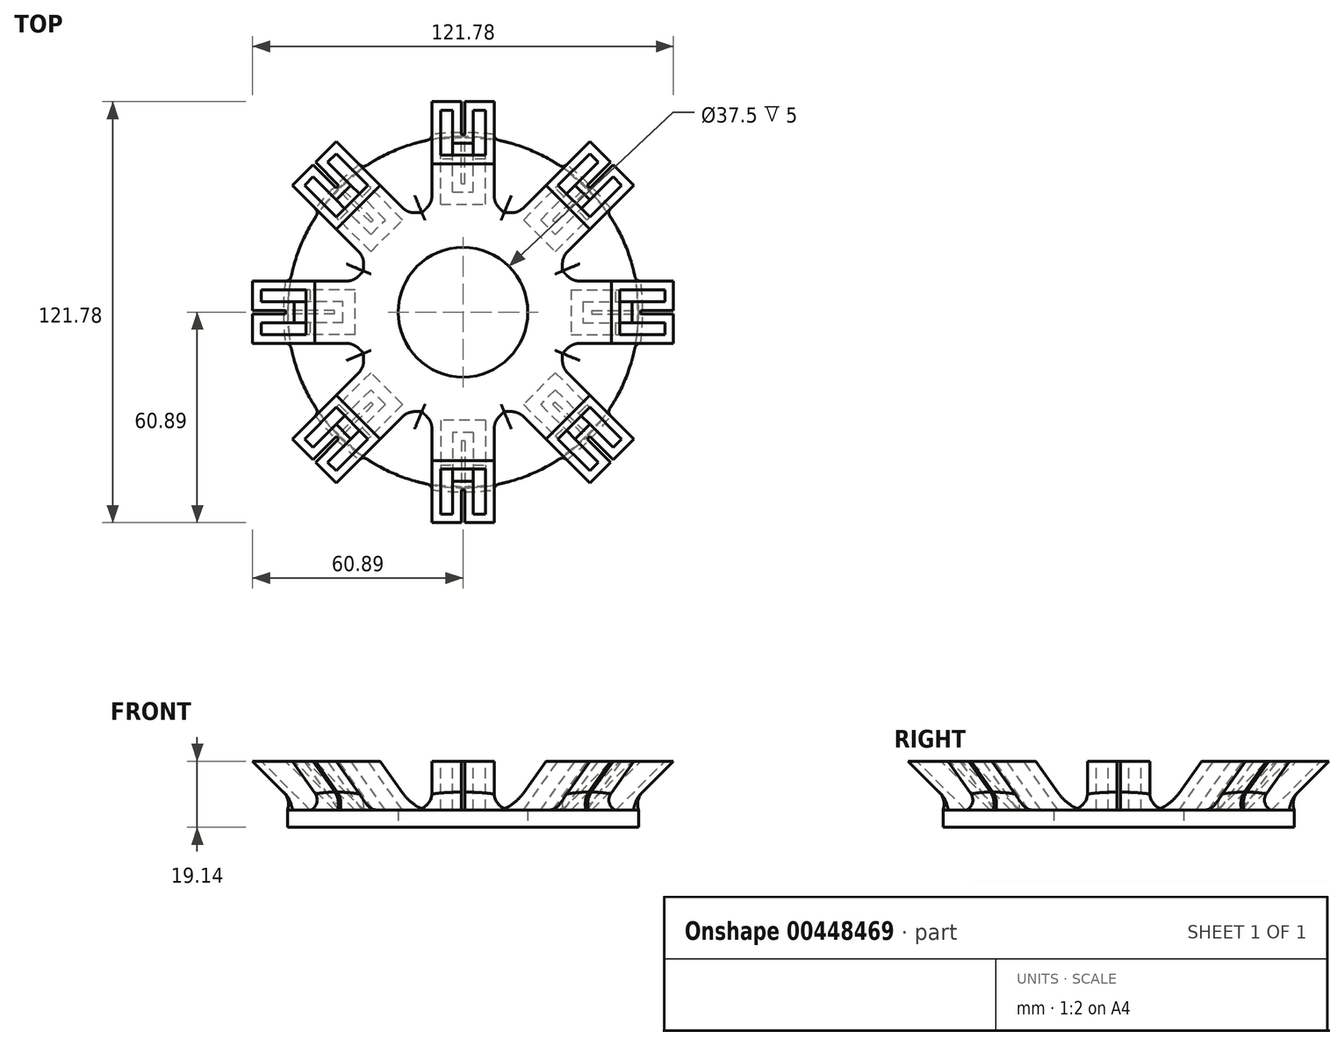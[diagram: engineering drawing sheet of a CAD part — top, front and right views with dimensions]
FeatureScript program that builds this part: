
annotation { "Feature Type Name" : "Feature", "Feature Type Description" : "" }
export const myFeature = defineFeature(function(context is Context, id is Id, definition is map)
    precondition{}
    {
        {
            var Q0;
            Q0=qCreatedBy(makeId("Top.planeOp"),FACE);
            var sketch = newSketch(context, id + "F0", { "sketchPlane" : qUnion([Q0])});
            skCircle(sketch, "E0", {"center": v(0, 0) * mm, "radius": 18.75 * mm});
            skCircle(sketch, "E1", {"center": v(0, 0) * mm, "radius": 50.8 * mm});
            skSolve(sketch);
        }
        {
            var Q0;
            Q0=makeQuery(id+"F0.imprint","IMPRINT",FACE,{"disambiguationData":[TD([[makeQuery(id+"F0.imprint","IMPRINT",EDGE,{"derivedFrom":sQuery(id+"F0.wireOp",EDGE,"E0")}),-1.0]])]});
            extrude(context, id + "F1", {"entities" : qUnion([Q0]), "depth" : 5 * mm});
        }
        {
            var Q0;
            Q0=makeQuery(id+"F1.opExtrude","CAP_FACE",FACE,{"disambiguationData":[OSD([sQuery(id+"F0.wireOp",EDGE,"E0"),sQuery(id+"F0.wireOp",EDGE,"E1")])],"isStart":false});
            var sketch = newSketch(context, id + "F2", { "sketchPlane" : qUnion([Q0])});
            skPoint(sketch, "E2", {"position": v(0, -31.75) * mm});
            skLineSegment(sketch, "E3", {"start": v(6, -31.75) * mm, "end": v(-6, -31.75) * mm});
            skLineSegment(sketch, "E4", {"start": v(6, -31.75) * mm, "end": v(6, -43.75) * mm});
            skLineSegment(sketch, "E5", {"start": v(-6, -31.75) * mm, "end": v(-6, -43.75) * mm});
            skLineSegment(sketch, "E6.0", {"start": v(-3.5, -34.25) * mm, "end": v(-3.5, -43.75) * mm});
            skLineSegment(sketch, "E6.1", {"start": v(3.5, -34.25) * mm, "end": v(-3.5, -34.25) * mm});
            skLineSegment(sketch, "E6.2", {"start": v(3.5, -34.25) * mm, "end": v(3.5, -43.75) * mm});
            skLineSegment(sketch, "E7", {"start": v(-6, -43.75) * mm, "end": v(-3.5, -43.75) * mm});
            skLineSegment(sketch, "E8", {"start": v(3.5, -43.75) * mm, "end": v(6, -43.75) * mm});
            skLineSegment(sketch, "E9.0", {"start": v(6.5, -31.25) * mm, "end": v(6.5, -44.25) * mm});
            skLineSegment(sketch, "E9.1", {"start": v(3, -44.25) * mm, "end": v(6.5, -44.25) * mm});
            skLineSegment(sketch, "E9.2", {"start": v(6.5, -31.25) * mm, "end": v(-6.5, -31.25) * mm});
            skLineSegment(sketch, "E9.3", {"start": v(3, -34.75) * mm, "end": v(3, -44.25) * mm});
            skLineSegment(sketch, "E9.4", {"start": v(-6.5, -31.25) * mm, "end": v(-6.5, -44.25) * mm});
            skLineSegment(sketch, "E9.5", {"start": v(-6.5, -44.25) * mm, "end": v(-3, -44.25) * mm});
            skLineSegment(sketch, "E9.6", {"start": v(-3, -34.75) * mm, "end": v(-3, -44.25) * mm});
            skLineSegment(sketch, "E9.7", {"start": v(3, -34.75) * mm, "end": v(-3, -34.75) * mm});
            skLineSegment(sketch, "E10.0", {"start": v(9, -28.75) * mm, "end": v(9, -46.75) * mm});
            skLineSegment(sketch, "E10.1", {"start": v(0.5, -46.75) * mm, "end": v(9, -46.75) * mm});
            skLineSegment(sketch, "E10.2", {"start": v(9, -28.75) * mm, "end": v(-9, -28.75) * mm});
            skLineSegment(sketch, "E10.3", {"start": v(0.5, -37.25) * mm, "end": v(0.5, -46.75) * mm});
            skLineSegment(sketch, "E10.4", {"start": v(-9, -28.75) * mm, "end": v(-9, -46.75) * mm});
            skLineSegment(sketch, "E10.5", {"start": v(-9, -46.75) * mm, "end": v(-0.5, -46.75) * mm});
            skLineSegment(sketch, "E10.6", {"start": v(-0.5, -37.25) * mm, "end": v(-0.5, -46.75) * mm});
            skLineSegment(sketch, "E10.7", {"start": v(0.5, -37.25) * mm, "end": v(-0.5, -37.25) * mm});
            skSolve(sketch);
        }
        {
            var Q0;
            Q0=qCreatedBy(makeId("Right.planeOp"),FACE);
            var sketch = newSketch(context, id + "F3", { "sketchPlane" : qUnion([Q0])});
            skPoint(sketch, "E11", {"position": v(-28.75, 5) * mm});
            skLineSegment(sketch, "E12", {"start": v(-28.75, 5) * mm, "end": v(-42.9, 19.14) * mm});
            skLineSegment(sketch, "E13", {"start": v(-28.75, 5) * mm, "end": v(-45.86, 5) * mm, "construction": true});
            skSolve(sketch);
        }
        {
            var Q0;
            Q0=makeQuery(id+"F2.imprint","IMPRINT",FACE,{"disambiguationData":[TD([[makeQuery(id+"F2.imprint","IMPRINT",EDGE,{"derivedFrom":sQuery(id+"F2.wireOp",EDGE,"E9.0")}),1.0]])]});
            var Q1;
            Q1=sQuery(id+"F3.wireOp",EDGE,"E12");
            sweep(context, id + "F4", {"operationType" : NewBodyOperationType.ADD, "profiles" : qUnion([Q0]), "path" : qUnion([Q1])});
        }
        {
            var Q0;
            Q0=qCreatedBy(makeId("Right.planeOp"),FACE);
            var sketch = newSketch(context, id + "F5", { "sketchPlane" : qUnion([Q0])});
            skLineSegment(sketch, "E14", {"start": v(0, 0) * mm, "end": v(0, 26.54) * mm, "construction": true});
            skSolve(sketch);
        }
        {
            var Q0;
            Q0=makeQuery(id+"F4.opSweep","CAP_EDGE",EDGE,{"disambiguationData":[OSD([sQuery(id+"F2.wireOp",EDGE,"E10.2"),sQuery(id+"F3.wireOp",VERTEX,"E12.start")])],"isStart":true});
            var Q1;
            Q1=makeQuery(id+"F4.opSweep","CAP_EDGE",EDGE,{"disambiguationData":[OSD([sQuery(id+"F2.wireOp",EDGE,"E10.0"),sQuery(id+"F3.wireOp",VERTEX,"E12.start")])],"isStart":true});
            var Q2;
            Q2=makeQuery(id+"F4.opSweep","CAP_EDGE",EDGE,{"disambiguationData":[OSD([sQuery(id+"F2.wireOp",EDGE,"E10.1"),sQuery(id+"F3.wireOp",VERTEX,"E12.start")])],"isStart":true});
            var Q3;
            Q3=makeQuery(id+"F4.opSweep","CAP_EDGE",EDGE,{"disambiguationData":[OSD([sQuery(id+"F2.wireOp",EDGE,"E10.5"),sQuery(id+"F3.wireOp",VERTEX,"E12.start")])],"isStart":true});
            var Q4;
            Q4=makeQuery(id+"F4.opSweep","CAP_EDGE",EDGE,{"disambiguationData":[OSD([sQuery(id+"F2.wireOp",EDGE,"E10.4"),sQuery(id+"F3.wireOp",VERTEX,"E12.start")])],"isStart":true});
            fillet(context, id + "F6", {"entities" : qUnion([Q0, Q1, Q2, Q3, Q4]), "radius" : 5 * mm, "tangentPropagation" : true, "allowEdgeOverflow" : false});
        }
        {
            var Q0;
            Q0=makeQuery(id+"F1.opExtrude","SWEPT_BODY",BODY,{"disambiguationData":[OSD([sQuery(id+"F0.wireOp",EDGE,"E0"),sQuery(id+"F0.wireOp",EDGE,"E1")])]});
            var Q1;
            Q1=sQuery(id+"F5.wireOp",EDGE,"E14");
            circularPattern(context, id + "F7", {"operationType" : NewBodyOperationType.ADD, "entities" : qUnion([Q0]), "axis" : qUnion([Q1]), "angle" : 360 * degree, "instanceCount" : 8, "equalSpace" : true});
        }
    });
